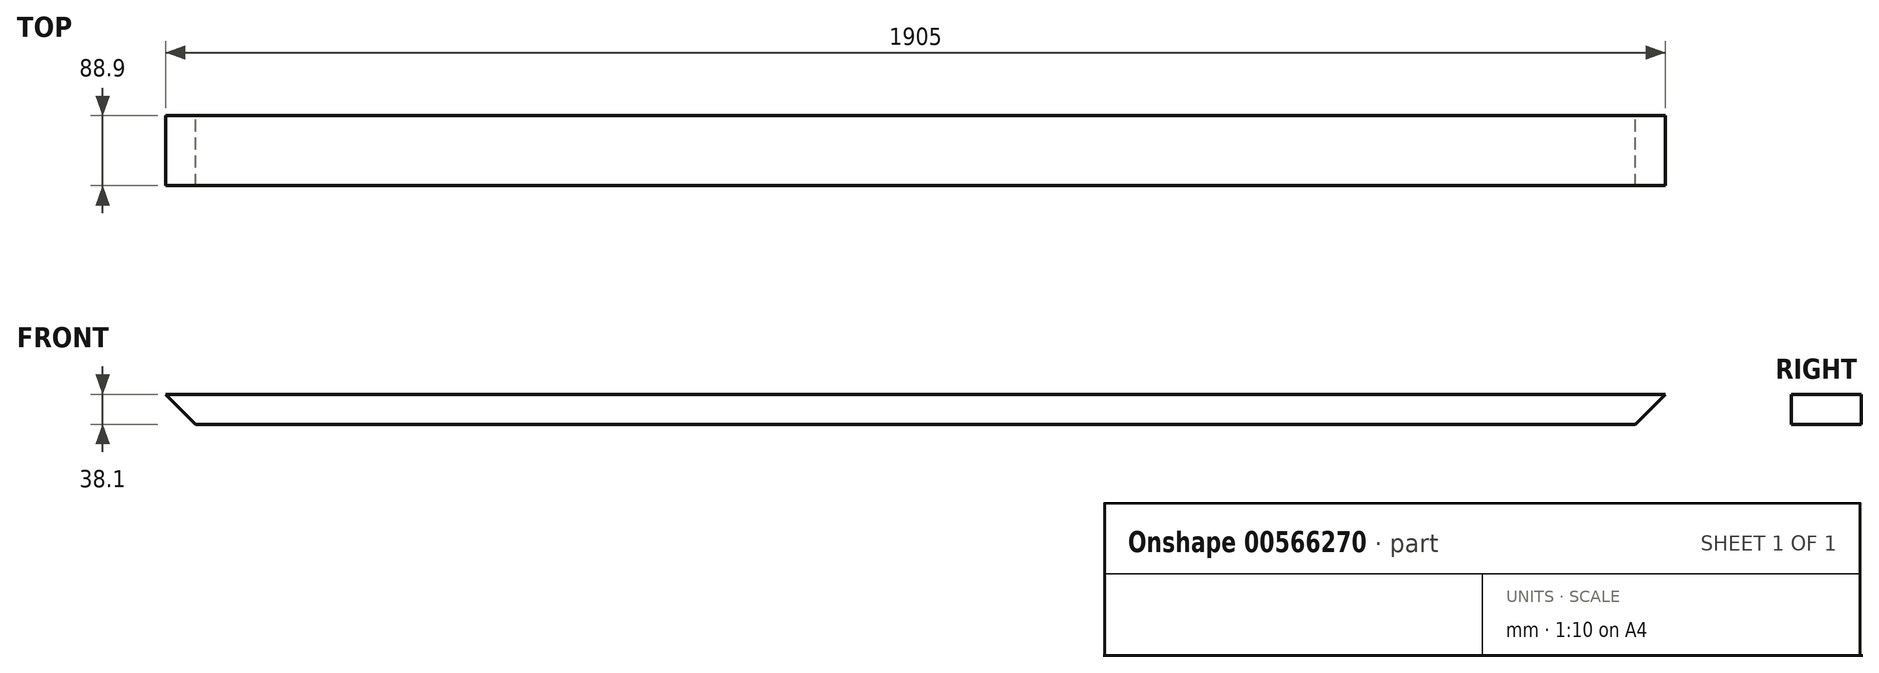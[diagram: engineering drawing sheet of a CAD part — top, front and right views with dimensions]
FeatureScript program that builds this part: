
annotation { "Feature Type Name" : "Feature", "Feature Type Description" : "" }
export const myFeature = defineFeature(function(context is Context, id is Id, definition is map)
    precondition{}
    {
        {
            var Q0;
            Q0=qCreatedBy(makeId("Front.planeOp"),FACE);
            var sketch = newSketch(context, id + "F0", { "sketchPlane" : qUnion([Q0])});
            skLineSegment(sketch, "E0", {"start": v(0, 0) * mm, "end": v(1905, 0) * mm});
            skLineSegment(sketch, "E1", {"start": v(1905, 0) * mm, "end": v(1866.9, -38.1) * mm});
            skLineSegment(sketch, "E2", {"start": v(1866.9, -38.1) * mm, "end": v(38.1, -38.1) * mm});
            skLineSegment(sketch, "E3", {"start": v(38.1, -38.1) * mm, "end": v(0, 0) * mm});
            skSolve(sketch);
        }
        {
            var Q0;
            Q0=makeQuery(id+"F0.imprint","IMPRINT",FACE,{"disambiguationData":[TD([[makeQuery(id+"F0.imprint","IMPRINT",EDGE,{"derivedFrom":sQuery(id+"F0.wireOp",EDGE,"E0")}),-1.0]])]});
            extrude(context, id + "F1", {"entities" : qUnion([Q0]), "depth" : 88.9 * mm, "offsetDistance" : 25.4 * mm});
        }
    });
